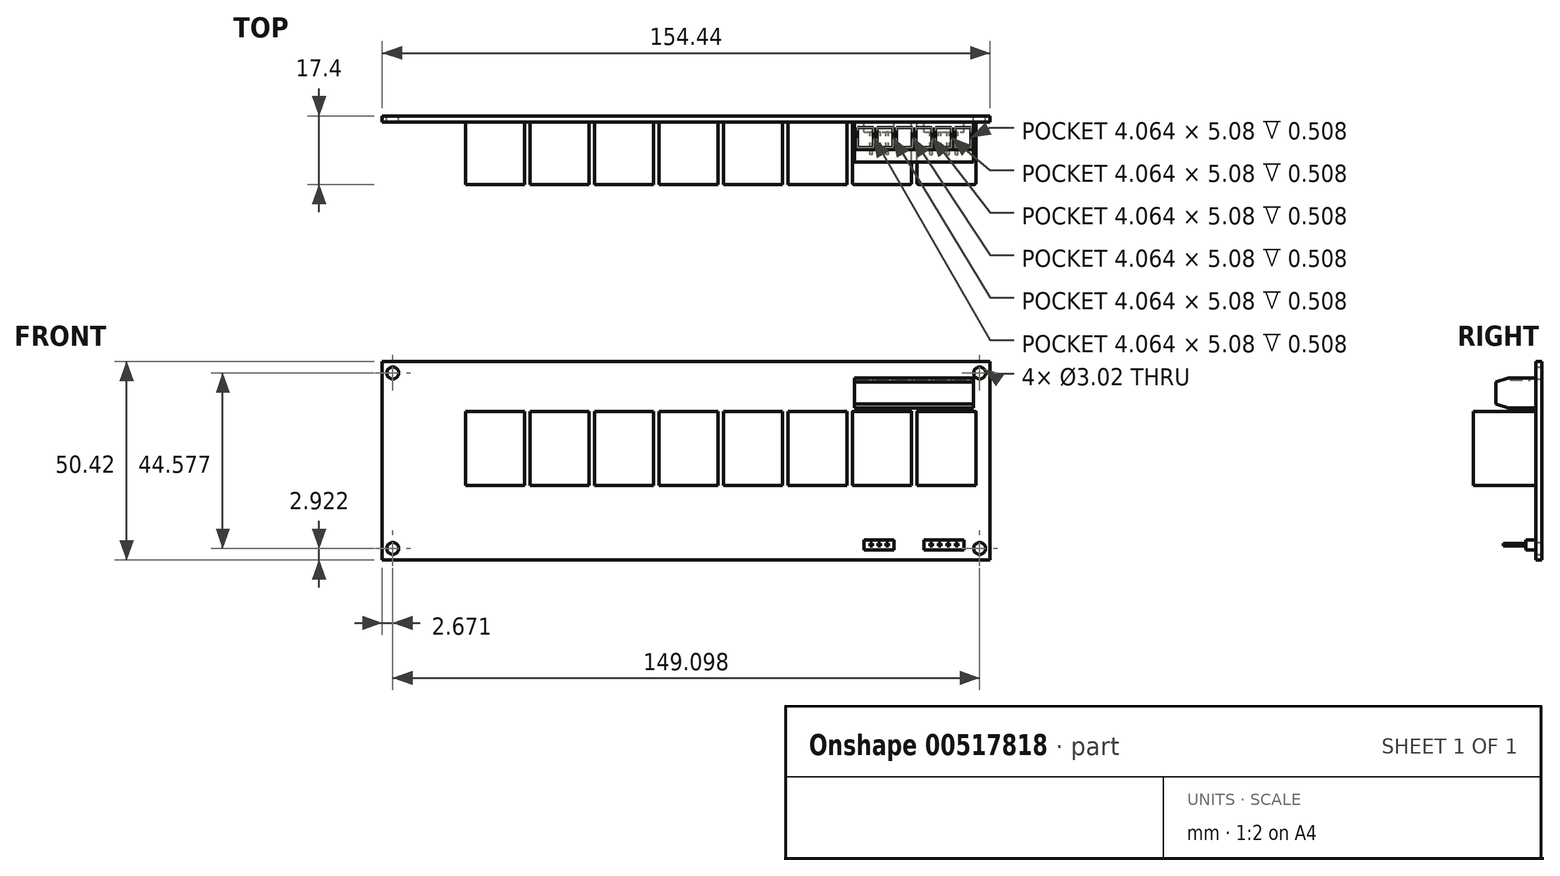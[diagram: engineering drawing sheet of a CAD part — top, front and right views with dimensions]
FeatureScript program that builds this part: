
annotation { "Feature Type Name" : "Feature", "Feature Type Description" : "" }
export const myFeature = defineFeature(function(context is Context, id is Id, definition is map)
    precondition{}
    {
        {
            var Q0;
            Q0=qCreatedBy(makeId("Front.planeOp"),FACE);
            var sketch = newSketch(context, id + "F0", { "sketchPlane" : qUnion([Q0])});
            skLineSegment(sketch, "E0.bottom", {"start": v(-77.22, 25.2) * mm, "end": v(77.22, 25.2) * mm});
            skLineSegment(sketch, "E0.top", {"start": v(-77.22, -25.2) * mm, "end": v(77.22, -25.2) * mm});
            skLineSegment(sketch, "E0.left", {"start": v(-77.22, 25.2) * mm, "end": v(-77.22, -25.2) * mm});
            skLineSegment(sketch, "E0.right", {"start": v(77.22, 25.2) * mm, "end": v(77.22, -25.2) * mm});
            skPoint(sketch, "E0.middle", {"position": v(0, 0) * mm});
            skLineSegment(sketch, "E1.bottom", {"start": v(74.55, 22.29) * mm, "end": v(-74.55, 22.29) * mm, "construction": true});
            skLineSegment(sketch, "E1.top", {"start": v(74.55, -22.29) * mm, "end": v(-74.55, -22.29) * mm, "construction": true});
            skLineSegment(sketch, "E1.left", {"start": v(74.55, 22.29) * mm, "end": v(74.55, -22.29) * mm, "construction": true});
            skLineSegment(sketch, "E1.right", {"start": v(-74.55, 22.29) * mm, "end": v(-74.55, -22.29) * mm, "construction": true});
            skCircle(sketch, "E2", {"center": v(-74.55, 22.29) * mm, "radius": 1.51 * mm});
            skCircle(sketch, "E3", {"center": v(74.55, 22.29) * mm, "radius": 1.51 * mm});
            skCircle(sketch, "E4", {"center": v(74.55, -22.29) * mm, "radius": 1.51 * mm});
            skCircle(sketch, "E5", {"center": v(-74.55, -22.29) * mm, "radius": 1.51 * mm});
            skSolve(sketch);
        }
        {
            var Q0;
            Q0=qSketchRegion(id+"F0",true);
            extrude(context, id + "F1", {"entities" : qUnion([Q0]), "depth" : 1.52 * mm});
        }
        {
            var Q0;
            Q0=makeQuery(id+"F1.opExtrude","CAP_FACE",FACE,{"disambiguationData":[OSD([sQuery(id+"F0.wireOp",EDGE,"E0.bottom"),sQuery(id+"F0.wireOp",EDGE,"E0.top"),sQuery(id+"F0.wireOp",EDGE,"E0.left"),sQuery(id+"F0.wireOp",EDGE,"E0.right"),sQuery(id+"F0.wireOp",EDGE,"E2"),sQuery(id+"F0.wireOp",EDGE,"E3"),sQuery(id+"F0.wireOp",EDGE,"E4"),sQuery(id+"F0.wireOp",EDGE,"E5")])],"isStart":false});
            var sketch = newSketch(context, id + "F2", { "sketchPlane" : qUnion([Q0])});
            skLineSegment(sketch, "E6.bottom", {"start": v(42.23, -6.29) * mm, "end": v(57.21, -6.29) * mm});
            skLineSegment(sketch, "E6.top", {"start": v(42.23, 12.5) * mm, "end": v(57.21, 12.5) * mm});
            skLineSegment(sketch, "E6.left", {"start": v(42.23, -6.29) * mm, "end": v(42.23, 12.5) * mm});
            skLineSegment(sketch, "E6.right", {"start": v(57.21, -6.29) * mm, "end": v(57.21, 12.5) * mm});
            skLineSegment(sketch, "E7.bottom", {"start": v(58.61, -6.29) * mm, "end": v(73.6, -6.29) * mm});
            skLineSegment(sketch, "E7.top", {"start": v(58.61, 12.5) * mm, "end": v(73.6, 12.5) * mm});
            skLineSegment(sketch, "E7.left", {"start": v(58.61, -6.29) * mm, "end": v(58.61, 12.5) * mm});
            skLineSegment(sketch, "E7.right", {"start": v(73.6, -6.29) * mm, "end": v(73.6, 12.5) * mm});
            skLineSegment(sketch, "E8", {"start": v(57.21, 0) * mm, "end": v(58.61, 0) * mm, "construction": true});
            skLineSegment(sketch, "E9.bottom", {"start": v(40.83, -6.29) * mm, "end": v(25.84, -6.29) * mm});
            skLineSegment(sketch, "E9.top", {"start": v(40.83, 12.5) * mm, "end": v(25.84, 12.5) * mm});
            skLineSegment(sketch, "E9.left", {"start": v(40.83, -6.29) * mm, "end": v(40.83, 12.5) * mm});
            skLineSegment(sketch, "E9.right", {"start": v(25.84, -6.29) * mm, "end": v(25.84, 12.5) * mm});
            skLineSegment(sketch, "E10.bottom", {"start": v(24.45, -6.29) * mm, "end": v(9.46, -6.29) * mm});
            skLineSegment(sketch, "E10.top", {"start": v(24.45, 12.5) * mm, "end": v(9.46, 12.5) * mm});
            skLineSegment(sketch, "E10.left", {"start": v(24.45, -6.29) * mm, "end": v(24.45, 12.5) * mm});
            skLineSegment(sketch, "E10.right", {"start": v(9.46, -6.29) * mm, "end": v(9.46, 12.5) * mm});
            skLineSegment(sketch, "E11.bottom", {"start": v(8.06, -6.29) * mm, "end": v(-6.92, -6.29) * mm});
            skLineSegment(sketch, "E11.top", {"start": v(8.06, 12.5) * mm, "end": v(-6.92, 12.5) * mm});
            skLineSegment(sketch, "E11.left", {"start": v(8.06, -6.29) * mm, "end": v(8.06, 12.5) * mm});
            skLineSegment(sketch, "E11.right", {"start": v(-6.92, -6.29) * mm, "end": v(-6.92, 12.5) * mm});
            skLineSegment(sketch, "E12.bottom", {"start": v(-8.32, -6.29) * mm, "end": v(-23.3, -6.29) * mm});
            skLineSegment(sketch, "E12.top", {"start": v(-8.32, 12.5) * mm, "end": v(-23.3, 12.5) * mm});
            skLineSegment(sketch, "E12.left", {"start": v(-8.32, -6.29) * mm, "end": v(-8.32, 12.5) * mm});
            skLineSegment(sketch, "E12.right", {"start": v(-23.3, -6.29) * mm, "end": v(-23.3, 12.5) * mm});
            skLineSegment(sketch, "E13.bottom", {"start": v(-24.7, -6.29) * mm, "end": v(-39.69, -6.29) * mm});
            skLineSegment(sketch, "E13.top", {"start": v(-24.7, 12.5) * mm, "end": v(-39.69, 12.5) * mm});
            skLineSegment(sketch, "E13.left", {"start": v(-24.7, -6.29) * mm, "end": v(-24.7, 12.5) * mm});
            skLineSegment(sketch, "E13.right", {"start": v(-39.69, -6.29) * mm, "end": v(-39.69, 12.5) * mm});
            skLineSegment(sketch, "E14.bottom", {"start": v(-41.08, -6.29) * mm, "end": v(-56.07, -6.29) * mm});
            skLineSegment(sketch, "E14.top", {"start": v(-41.08, 12.5) * mm, "end": v(-56.07, 12.5) * mm});
            skLineSegment(sketch, "E14.left", {"start": v(-41.08, -6.29) * mm, "end": v(-41.08, 12.5) * mm});
            skLineSegment(sketch, "E14.right", {"start": v(-56.07, -6.29) * mm, "end": v(-56.07, 12.5) * mm});
            skLineSegment(sketch, "E15", {"start": v(-41.08, -6.29) * mm, "end": v(-39.69, -6.29) * mm, "construction": true});
            skLineSegment(sketch, "E16", {"start": v(-24.7, -6.29) * mm, "end": v(-23.3, -6.29) * mm, "construction": true});
            skLineSegment(sketch, "E17", {"start": v(-8.32, -6.29) * mm, "end": v(-6.92, -6.29) * mm, "construction": true});
            skLineSegment(sketch, "E18", {"start": v(8.06, -6.29) * mm, "end": v(9.46, -6.29) * mm, "construction": true});
            skLineSegment(sketch, "E19", {"start": v(24.45, -6.29) * mm, "end": v(25.84, -6.29) * mm, "construction": true});
            skLineSegment(sketch, "E20", {"start": v(40.83, -6.29) * mm, "end": v(42.23, -6.29) * mm, "construction": true});
            skLineSegment(sketch, "E21", {"start": v(57.21, -6.29) * mm, "end": v(58.61, -6.29) * mm, "construction": true});
            skSolve(sketch);
        }
        {
            var Q0;
            Q0=qSketchRegion(id+"F2",true);
            extrude(context, id + "F3", {"entities" : qUnion([Q0]), "operationType" : NewBodyOperationType.ADD, "depth" : 15.88 * mm, "offsetDistance" : 25.4 * mm});
        }
        {
            var Q0;
            Q0=makeQuery(id+"F3.opExtrude","CAP_FACE",FACE,{"disambiguationData":[OSD([sQuery(id+"F2.wireOp",EDGE,"E6.bottom"),sQuery(id+"F2.wireOp",EDGE,"E6.top"),sQuery(id+"F2.wireOp",EDGE,"E6.left"),sQuery(id+"F2.wireOp",EDGE,"E6.right")])],"isStart":false});
            var Q1;
            Q1=makeQuery(id+"F3.opExtrude","CAP_FACE",FACE,{"disambiguationData":[OSD([sQuery(id+"F2.wireOp",EDGE,"E7.bottom"),sQuery(id+"F2.wireOp",EDGE,"E7.top"),sQuery(id+"F2.wireOp",EDGE,"E7.left"),sQuery(id+"F2.wireOp",EDGE,"E7.right")])],"isStart":false});
            fillet(context, id + "F4", {"entities" : qUnion([Q0, Q1]), "radius" : 0.38 * mm, "tangentPropagation" : true, "allowEdgeOverflow" : false});
        }
        {
            var Q0;
            Q0=makeQuery(id+"F1.opExtrude","CAP_FACE",FACE,{"disambiguationData":[OSD([sQuery(id+"F0.wireOp",EDGE,"E0.bottom"),sQuery(id+"F0.wireOp",EDGE,"E0.top"),sQuery(id+"F0.wireOp",EDGE,"E0.left"),sQuery(id+"F0.wireOp",EDGE,"E0.right"),sQuery(id+"F0.wireOp",EDGE,"E2"),sQuery(id+"F0.wireOp",EDGE,"E3"),sQuery(id+"F0.wireOp",EDGE,"E4"),sQuery(id+"F0.wireOp",EDGE,"E5")])],"isStart":false});
            var sketch = newSketch(context, id + "F5", { "sketchPlane" : qUnion([Q0])});
            skLineSegment(sketch, "E22.bottom", {"start": v(42.8, 13.4) * mm, "end": v(73.03, 13.4) * mm});
            skLineSegment(sketch, "E22.top", {"start": v(42.8, 21.02) * mm, "end": v(73.03, 21.02) * mm});
            skLineSegment(sketch, "E22.left", {"start": v(42.8, 13.4) * mm, "end": v(42.8, 21.02) * mm});
            skLineSegment(sketch, "E22.right", {"start": v(73.03, 13.4) * mm, "end": v(73.03, 21.02) * mm});
            skSolve(sketch);
        }
        {
            var Q0;
            Q0=qSketchRegion(id+"F5",true);
            extrude(context, id + "F6", {"entities" : qUnion([Q0]), "operationType" : NewBodyOperationType.ADD, "depth" : 10.16 * mm});
        }
        {
            var Q0;
            Q0=makeQuery(id+"F6.opExtrude","CAP_EDGE",EDGE,{"disambiguationData":[OSD([sQuery(id+"F5.wireOp",EDGE,"E22.top")])],"isStart":false});
            var Q1;
            Q1=makeQuery(id+"F6.opExtrude","CAP_EDGE",EDGE,{"disambiguationData":[OSD([sQuery(id+"F5.wireOp",EDGE,"E22.bottom")])],"isStart":false});
            chamfer(context, id + "F7", {"entities" : qUnion([Q0, Q1]), "chamferType" : ChamferType.TWO_OFFSETS, "width1" : 3.17 * mm, "oppositeDirection" : false, "width2" : 1.02 * mm, "tangentPropagation" : true});
        }
        {
            var Q0;
            Q0=makeQuery(id+"F6.opExtrude","SWEPT_FACE",FACE,{"disambiguationData":[OSD([sQuery(id+"F5.wireOp",EDGE,"E22.top")])]});
            var sketch = newSketch(context, id + "F8", { "sketchPlane" : qUnion([Q0])});
            skLineSegment(sketch, "E23.bottom", {"start": v(43.5, -8) * mm, "end": v(47.56, -8) * mm});
            skLineSegment(sketch, "E23.top", {"start": v(43.5, -2.92) * mm, "end": v(47.56, -2.92) * mm});
            skLineSegment(sketch, "E23.left", {"start": v(43.5, -8) * mm, "end": v(43.5, -2.92) * mm});
            skLineSegment(sketch, "E23.right", {"start": v(47.56, -8) * mm, "end": v(47.56, -2.92) * mm});
            skLineSegment(sketch, "E24.bottom", {"start": v(48.45, -8) * mm, "end": v(52.51, -8) * mm});
            skLineSegment(sketch, "E24.top", {"start": v(48.45, -2.92) * mm, "end": v(52.51, -2.92) * mm});
            skLineSegment(sketch, "E24.left", {"start": v(48.45, -8) * mm, "end": v(48.45, -2.92) * mm});
            skLineSegment(sketch, "E24.right", {"start": v(52.51, -8) * mm, "end": v(52.51, -2.92) * mm});
            skLineSegment(sketch, "E25.bottom", {"start": v(53.4, -8) * mm, "end": v(57.47, -8) * mm});
            skLineSegment(sketch, "E25.top", {"start": v(53.4, -2.92) * mm, "end": v(57.47, -2.92) * mm});
            skLineSegment(sketch, "E25.left", {"start": v(53.4, -8) * mm, "end": v(53.4, -2.92) * mm});
            skLineSegment(sketch, "E25.right", {"start": v(57.47, -8) * mm, "end": v(57.47, -2.92) * mm});
            skLineSegment(sketch, "E26", {"start": v(47.56, -2.92) * mm, "end": v(48.45, -2.92) * mm, "construction": true});
            skLineSegment(sketch, "E27", {"start": v(52.51, -2.92) * mm, "end": v(53.4, -2.92) * mm, "construction": true});
            skLineSegment(sketch, "E28.bottom", {"start": v(58.36, -8) * mm, "end": v(62.42, -8) * mm});
            skLineSegment(sketch, "E28.top", {"start": v(58.36, -2.92) * mm, "end": v(62.42, -2.92) * mm});
            skLineSegment(sketch, "E28.left", {"start": v(58.36, -8) * mm, "end": v(58.36, -2.92) * mm});
            skLineSegment(sketch, "E28.right", {"start": v(62.42, -8) * mm, "end": v(62.42, -2.92) * mm});
            skLineSegment(sketch, "E29.bottom", {"start": v(63.3, -8) * mm, "end": v(67.37, -8) * mm});
            skLineSegment(sketch, "E29.top", {"start": v(63.3, -2.92) * mm, "end": v(67.37, -2.92) * mm});
            skLineSegment(sketch, "E29.left", {"start": v(63.3, -8) * mm, "end": v(63.3, -2.92) * mm});
            skLineSegment(sketch, "E29.right", {"start": v(67.37, -8) * mm, "end": v(67.37, -2.92) * mm});
            skLineSegment(sketch, "E30.bottom", {"start": v(68.26, -8) * mm, "end": v(72.33, -8) * mm});
            skLineSegment(sketch, "E30.top", {"start": v(68.26, -2.92) * mm, "end": v(72.33, -2.92) * mm});
            skLineSegment(sketch, "E30.left", {"start": v(68.26, -8) * mm, "end": v(68.26, -2.92) * mm});
            skLineSegment(sketch, "E30.right", {"start": v(72.33, -8) * mm, "end": v(72.33, -2.92) * mm});
            skLineSegment(sketch, "E31", {"start": v(57.47, -2.92) * mm, "end": v(58.36, -2.92) * mm, "construction": true});
            skLineSegment(sketch, "E32", {"start": v(62.42, -2.92) * mm, "end": v(63.3, -2.92) * mm, "construction": true});
            skLineSegment(sketch, "E33", {"start": v(67.37, -2.92) * mm, "end": v(68.26, -2.92) * mm, "construction": true});
            skLineSegment(sketch, "E34", {"start": v(43.5, -8) * mm, "end": v(42.8, -8) * mm, "construction": true});
            skLineSegment(sketch, "E35", {"start": v(72.33, -8) * mm, "end": v(73.03, -8) * mm, "construction": true});
            skSolve(sketch);
        }
        {
            var Q0;
            Q0=qSketchRegion(id+"F8",true);
            extrude(context, id + "F9", {"entities" : qUnion([Q0]), "operationType" : NewBodyOperationType.REMOVE, "oppositeDirection" : true, "depth" : 0.5 * mm});
        }
        {
            var Q0;
            Q0=makeQuery(id+"F1.opExtrude","CAP_FACE",FACE,{"disambiguationData":[OSD([sQuery(id+"F0.wireOp",EDGE,"E0.bottom"),sQuery(id+"F0.wireOp",EDGE,"E0.top"),sQuery(id+"F0.wireOp",EDGE,"E0.left"),sQuery(id+"F0.wireOp",EDGE,"E0.right"),sQuery(id+"F0.wireOp",EDGE,"E2"),sQuery(id+"F0.wireOp",EDGE,"E3"),sQuery(id+"F0.wireOp",EDGE,"E4"),sQuery(id+"F0.wireOp",EDGE,"E5")])],"isStart":false});
            var sketch = newSketch(context, id + "F10", { "sketchPlane" : qUnion([Q0])});
            skLineSegment(sketch, "E36.bottom", {"start": v(45.21, -22.67) * mm, "end": v(52.83, -22.67) * mm});
            skLineSegment(sketch, "E36.top", {"start": v(45.21, -20.13) * mm, "end": v(52.83, -20.13) * mm});
            skLineSegment(sketch, "E36.left", {"start": v(45.21, -22.67) * mm, "end": v(45.21, -20.13) * mm});
            skLineSegment(sketch, "E36.right", {"start": v(52.83, -22.67) * mm, "end": v(52.83, -20.13) * mm});
            skLineSegment(sketch, "E37.bottom", {"start": v(60.45, -22.67) * mm, "end": v(70.61, -22.67) * mm});
            skLineSegment(sketch, "E37.top", {"start": v(60.45, -20.13) * mm, "end": v(70.61, -20.13) * mm});
            skLineSegment(sketch, "E37.left", {"start": v(60.45, -22.67) * mm, "end": v(60.45, -20.13) * mm});
            skLineSegment(sketch, "E37.right", {"start": v(70.61, -22.67) * mm, "end": v(70.61, -20.13) * mm});
            skSolve(sketch);
        }
        {
            var Q0;
            Q0=qSketchRegion(id+"F10",true);
            extrude(context, id + "F11", {"entities" : qUnion([Q0]), "operationType" : NewBodyOperationType.ADD, "depth" : 2.54 * mm});
        }
        {
            var Q0;
            Q0=makeQuery(id+"F11.opExtrude","CAP_FACE",FACE,{"disambiguationData":[OSD([sQuery(id+"F10.wireOp",EDGE,"E37.bottom"),sQuery(id+"F10.wireOp",EDGE,"E37.top"),sQuery(id+"F10.wireOp",EDGE,"E37.left"),sQuery(id+"F10.wireOp",EDGE,"E37.right")])],"isStart":false});
            var sketch = newSketch(context, id + "F12", { "sketchPlane" : qUnion([Q0])});
            skLineSegment(sketch, "E38.bottom", {"start": v(61.98, -21.72) * mm, "end": v(62.61, -21.72) * mm});
            skLineSegment(sketch, "E38.top", {"start": v(61.98, -21.08) * mm, "end": v(62.61, -21.08) * mm});
            skLineSegment(sketch, "E38.left", {"start": v(61.98, -21.72) * mm, "end": v(61.98, -21.08) * mm});
            skLineSegment(sketch, "E38.right", {"start": v(62.61, -21.72) * mm, "end": v(62.61, -21.08) * mm});
            skLineSegment(sketch, "E39.bottom", {"start": v(64.14, -21.72) * mm, "end": v(64.77, -21.72) * mm});
            skLineSegment(sketch, "E39.top", {"start": v(64.14, -21.08) * mm, "end": v(64.77, -21.08) * mm});
            skLineSegment(sketch, "E39.left", {"start": v(64.14, -21.72) * mm, "end": v(64.14, -21.08) * mm});
            skLineSegment(sketch, "E39.right", {"start": v(64.77, -21.72) * mm, "end": v(64.77, -21.08) * mm});
            skLineSegment(sketch, "E40.bottom", {"start": v(66.3, -21.72) * mm, "end": v(66.93, -21.72) * mm});
            skLineSegment(sketch, "E40.top", {"start": v(66.3, -21.08) * mm, "end": v(66.93, -21.08) * mm});
            skLineSegment(sketch, "E40.left", {"start": v(66.3, -21.72) * mm, "end": v(66.3, -21.08) * mm});
            skLineSegment(sketch, "E40.right", {"start": v(66.93, -21.72) * mm, "end": v(66.93, -21.08) * mm});
            skLineSegment(sketch, "E41.bottom", {"start": v(68.45, -21.72) * mm, "end": v(69.09, -21.72) * mm});
            skLineSegment(sketch, "E41.top", {"start": v(68.45, -21.08) * mm, "end": v(69.09, -21.08) * mm});
            skLineSegment(sketch, "E41.left", {"start": v(68.45, -21.72) * mm, "end": v(68.45, -21.08) * mm});
            skLineSegment(sketch, "E41.right", {"start": v(69.09, -21.72) * mm, "end": v(69.09, -21.08) * mm});
            skLineSegment(sketch, "E42", {"start": v(60.45, -21.4) * mm, "end": v(61.98, -21.4) * mm, "construction": true});
            skLineSegment(sketch, "E43", {"start": v(62.61, -21.4) * mm, "end": v(64.14, -21.4) * mm, "construction": true});
            skLineSegment(sketch, "E44", {"start": v(69.09, -21.4) * mm, "end": v(70.61, -21.4) * mm, "construction": true});
            skLineSegment(sketch, "E45", {"start": v(64.77, -21.4) * mm, "end": v(66.3, -21.4) * mm, "construction": true});
            skLineSegment(sketch, "E46", {"start": v(66.93, -21.4) * mm, "end": v(68.45, -21.4) * mm, "construction": true});
            skLineSegment(sketch, "E47.bottom", {"start": v(51.4, -21.72) * mm, "end": v(50.77, -21.72) * mm});
            skLineSegment(sketch, "E47.top", {"start": v(51.4, -21.08) * mm, "end": v(50.77, -21.08) * mm});
            skLineSegment(sketch, "E47.left", {"start": v(51.4, -21.72) * mm, "end": v(51.4, -21.08) * mm});
            skLineSegment(sketch, "E47.right", {"start": v(50.77, -21.72) * mm, "end": v(50.77, -21.08) * mm});
            skLineSegment(sketch, "E48.bottom", {"start": v(49.34, -21.72) * mm, "end": v(48.7, -21.72) * mm});
            skLineSegment(sketch, "E48.top", {"start": v(49.34, -21.08) * mm, "end": v(48.7, -21.08) * mm});
            skLineSegment(sketch, "E48.left", {"start": v(49.34, -21.72) * mm, "end": v(49.34, -21.08) * mm});
            skLineSegment(sketch, "E48.right", {"start": v(48.7, -21.72) * mm, "end": v(48.7, -21.08) * mm});
            skLineSegment(sketch, "E49.bottom", {"start": v(47.28, -21.72) * mm, "end": v(46.64, -21.72) * mm});
            skLineSegment(sketch, "E49.top", {"start": v(47.28, -21.08) * mm, "end": v(46.64, -21.08) * mm});
            skLineSegment(sketch, "E49.left", {"start": v(47.28, -21.72) * mm, "end": v(47.28, -21.08) * mm});
            skLineSegment(sketch, "E49.right", {"start": v(46.64, -21.72) * mm, "end": v(46.64, -21.08) * mm});
            skLineSegment(sketch, "E50", {"start": v(49.34, -21.4) * mm, "end": v(50.77, -21.4) * mm, "construction": true});
            skLineSegment(sketch, "E51", {"start": v(48.7, -21.4) * mm, "end": v(47.28, -21.4) * mm, "construction": true});
            skLineSegment(sketch, "E52", {"start": v(46.64, -21.4) * mm, "end": v(45.21, -21.4) * mm, "construction": true});
            skLineSegment(sketch, "E53", {"start": v(51.4, -21.4) * mm, "end": v(52.83, -21.4) * mm, "construction": true});
            skSolve(sketch);
        }
        {
            var Q0;
            Q0=qSketchRegion(id+"F12",true);
            extrude(context, id + "F13", {"entities" : qUnion([Q0]), "operationType" : NewBodyOperationType.ADD, "depth" : 5.7 * mm});
        }
    });
